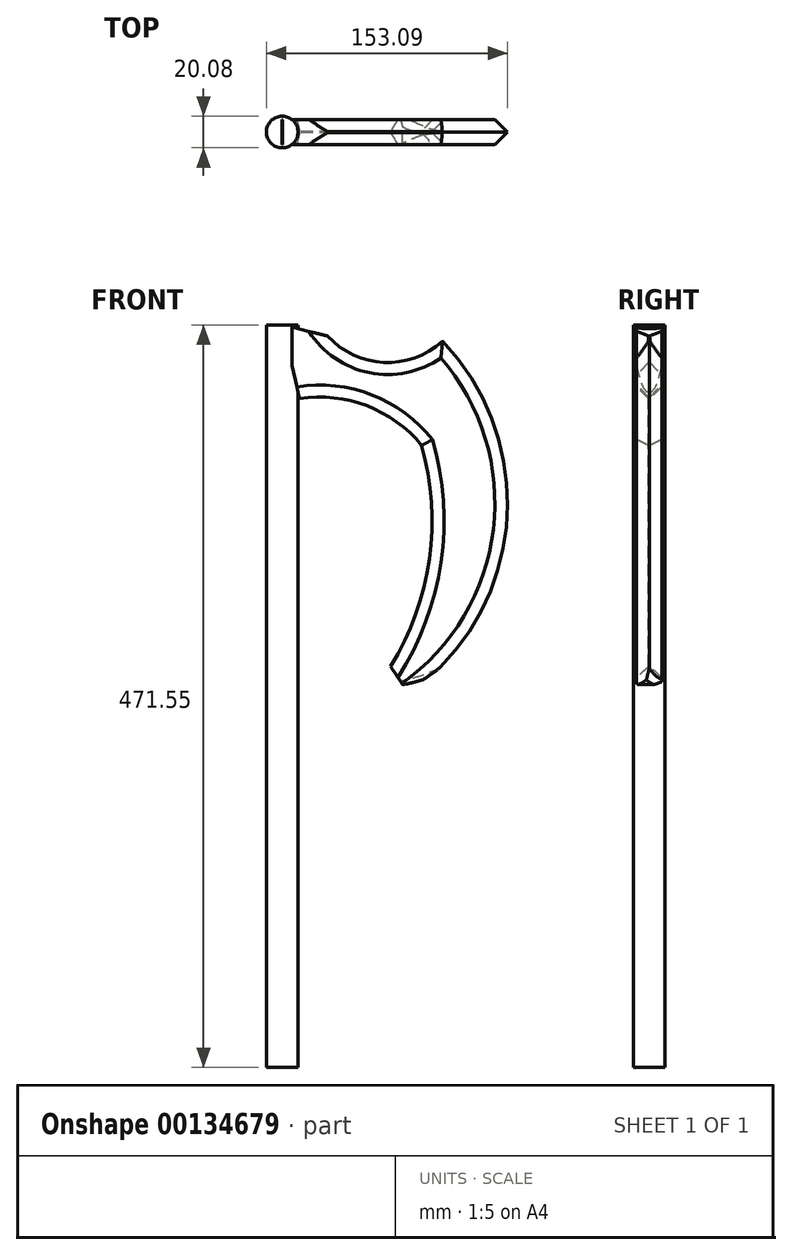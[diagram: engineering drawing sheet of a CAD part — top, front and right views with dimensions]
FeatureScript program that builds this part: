
annotation { "Feature Type Name" : "Feature", "Feature Type Description" : "" }
export const myFeature = defineFeature(function(context is Context, id is Id, definition is map)
    precondition{}
    {
        {
            var Q0;
            Q0=qCreatedBy(makeId("Top.planeOp"),FACE);
            var sketch = newSketch(context, id + "F0", { "sketchPlane" : qUnion([Q0])});
            skCircle(sketch, "E0", {"center": v(0, 0) * mm, "radius": 10.04 * mm});
            skSolve(sketch);
        }
        {
            var Q0;
            Q0 = qSketchRegion(id + "F0", true);
            extrude(context, id + "F1", {"entities" : qUnion([Q0]), "depth" : 471.5 * mm});
        }
        {
            var Q0;
            Q0=qCreatedBy(makeId("Front.planeOp"),FACE);
            var sketch = newSketch(context, id + "F2", { "sketchPlane" : qUnion([Q0])});
            skLineSegment(sketch, "E1", {"start": v(0, 471.55) * mm, "end": v(28.77, 464.55) * mm});
            skArc(sketch, "E2", {"start": v(28.77, 464.55) * mm, "mid": v(67, 447.7) * mm, "end": v(105.23, 464.55) * mm});
            skArc(sketch, "E3", {"start": v(111.16, 258.86) * mm, "mid": v(147.71, 362.84) * mm, "end": v(105.23, 464.55) * mm});
            skArc(sketch, "E4", {"start": v(88.54, 395.1) * mm, "mid": v(53.7, 420.18) * mm, "end": v(11, 424.7) * mm});
            skLineSegment(sketch, "E5", {"start": v(0, 471.55) * mm, "end": v(11, 424.7) * mm});
            skArc(sketch, "E6", {"start": v(60.89, 242.82) * mm, "mid": v(87.68, 245.66) * mm, "end": v(111.16, 258.86) * mm});
            skArc(sketch, "E7", {"start": v(60.89, 242.82) * mm, "mid": v(92.3, 315.76) * mm, "end": v(88.54, 395.1) * mm});
            skSolve(sketch);
        }
        {
            var Q0;
            Q0=makeQuery(id+"F2.imprint","IMPRINT",FACE,{"disambiguationData":[TD([[makeQuery(id+"F2.imprint","IMPRINT",EDGE,{"derivedFrom":sQuery(id+"F2.wireOp",EDGE,"E1")}),-1.0]])]});
            extrude(context, id + "F3", {"entities" : qUnion([Q0]), "operationType" : NewBodyOperationType.ADD, "depth" : 7.98 * mm, "hasSecondDirection" : true, "secondDirectionOppositeDirection" : true, "secondDirectionDepth" : 7.97 * mm});
        }
        {
            var Q0;
            Q0=makeQuery(id+"F3.opExtrude","CAP_EDGE",EDGE,{"disambiguationData":[OSD([sQuery(id+"F2.wireOp",EDGE,"E3")])],"isStart":false});
            var Q1;
            Q1=makeQuery(id+"F3.opExtrude","CAP_EDGE",EDGE,{"disambiguationData":[OSD([sQuery(id+"F2.wireOp",EDGE,"E3")])],"isStart":true});
            chamfer(context, id + "F4", {"entities" : qUnion([Q0, Q1]), "width" : 12.7 * mm, "tangentPropagation" : true});
        }
        {
            var Q0;
            Q0=makeQuery(id+"F3.opExtrude","CAP_EDGE",EDGE,{"disambiguationData":[OSD([sQuery(id+"F2.wireOp",EDGE,"E7")])],"isStart":false});
            var Q1;
            Q1=makeQuery(id+"F3.opExtrude","CAP_EDGE",EDGE,{"disambiguationData":[OSD([sQuery(id+"F2.wireOp",EDGE,"E7")])],"isStart":true});
            var Q2;
            Q2=makeQuery(id+"F3.opExtrude","SWEPT_EDGE",EDGE,{"disambiguationData":[OSD([sQuery(id+"F2.wireOp",EDGE,"E6"),sQuery(id+"F2.wireOp",EDGE,"E7")])]});
            var Q3;
            Q3=makeQuery(id+"F4.opChamfer","BLEND_EDGE",EDGE,{"blendedFrom":[makeQuery(id+"F3.opExtrude","CAP_EDGE",EDGE,{"disambiguationData":[OSD([sQuery(id+"F2.wireOp",EDGE,"E3")])],"isStart":true}),makeQuery(id+"F3.opExtrude","SWEPT_FACE",FACE,{"disambiguationData":[OSD([sQuery(id+"F2.wireOp",EDGE,"E6")])]})],"blendedInto":[makeQuery(id+"F3.opExtrude","SWEPT_FACE",FACE,{"disambiguationData":[OSD([sQuery(id+"F2.wireOp",EDGE,"E6")])]})]});
            var Q4;
            Q4=makeQuery(id+"F3.opExtrude","CAP_EDGE",EDGE,{"disambiguationData":[OSD([sQuery(id+"F2.wireOp",EDGE,"E4")])],"isStart":false});
            var Q5;
            Q5=makeQuery(id+"F3.opExtrude","CAP_EDGE",EDGE,{"disambiguationData":[OSD([sQuery(id+"F2.wireOp",EDGE,"E4")])],"isStart":true});
            var Q6;
            Q6=makeQuery(id+"F3.opExtrude","CAP_EDGE",EDGE,{"disambiguationData":[OSD([sQuery(id+"F2.wireOp",EDGE,"E2")])],"isStart":false});
            var Q7;
            Q7=makeQuery(id+"F3.opExtrude","CAP_EDGE",EDGE,{"disambiguationData":[OSD([sQuery(id+"F2.wireOp",EDGE,"E2")])],"isStart":true});
            chamfer(context, id + "F5", {"entities" : qUnion([Q0, Q1, Q2, Q3, Q4, Q5, Q6, Q7]), "width" : 7.62 * mm, "tangentPropagation" : true});
        }
    });
